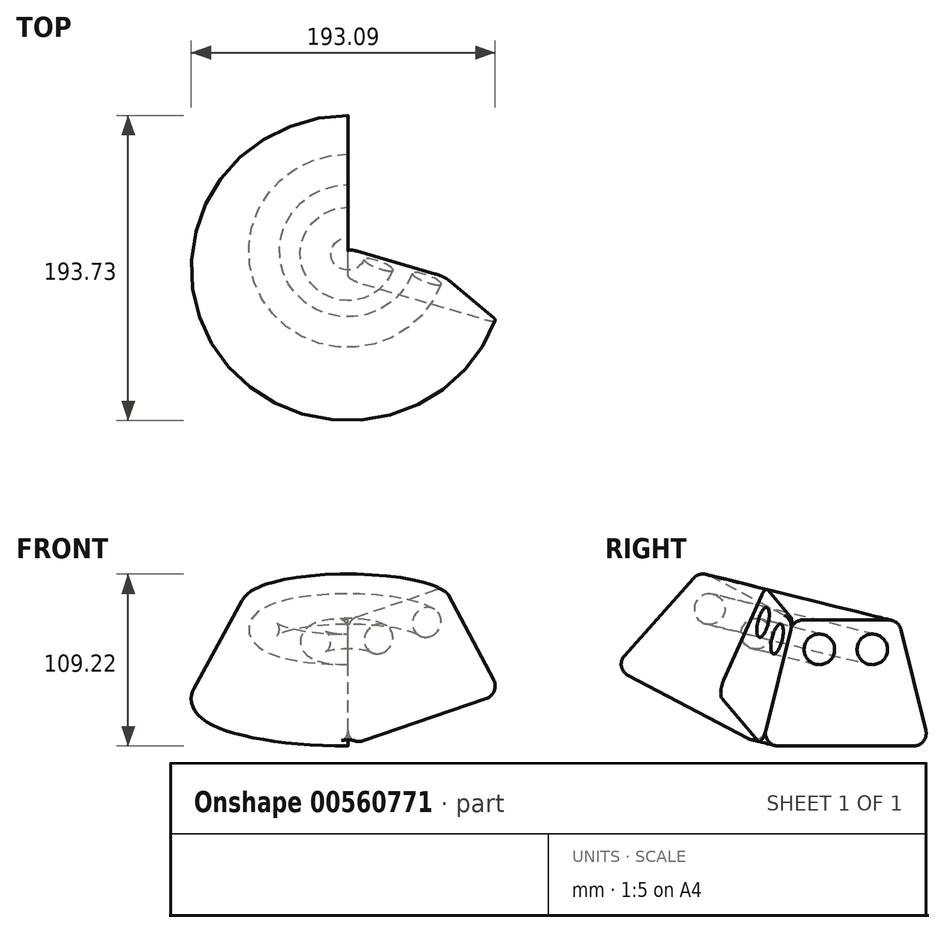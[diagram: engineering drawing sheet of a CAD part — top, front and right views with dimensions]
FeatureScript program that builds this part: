
annotation { "Feature Type Name" : "Feature", "Feature Type Description" : "" }
export const myFeature = defineFeature(function(context is Context, id is Id, definition is map)
    precondition{}
    {
        {
            var Q0;
            Q0=qCreatedBy(makeId("Right.planeOp"),FACE);
            var sketch = newSketch(context, id + "F0", { "sketchPlane" : qUnion([Q0])});
            skLineSegment(sketch, "E0.bottom", {"start": v(10.22, 0) * mm, "end": v(96.29, 0) * mm});
            skLineSegment(sketch, "E0.top", {"start": v(26.06, 80.02) * mm, "end": v(80.44, 80.02) * mm});
            skLineSegment(sketch, "E0.left", {"start": v(2.46, 9.92) * mm, "end": v(18.3, 73.94) * mm});
            skLineSegment(sketch, "E0.right", {"start": v(104.05, 9.92) * mm, "end": v(88.21, 73.94) * mm});
            skLineSegment(sketch, "E1", {"start": v(53.25, 80.02) * mm, "end": v(53.25, 0) * mm, "construction": true});
            skCircle(sketch, "E2", {"center": v(36.46, 61.35) * mm, "radius": 9.7 * mm});
            skCircle(sketch, "E3.MirrorC", {"center": v(70.05, 61.35) * mm, "radius": 9.7 * mm});
            skPoint(sketch, "E4.visualSharp", {"position": v(106.5, 0) * mm});
            skArc(sketch, "E4.filletArc", {"start": v(96.29, 0) * mm, "mid": v(102.59, 3.07) * mm, "end": v(104.05, 9.92) * mm});
            skPoint(sketch, "E5.visualSharp", {"position": v(0, 0) * mm});
            skArc(sketch, "E5.filletArc", {"start": v(2.46, 9.92) * mm, "mid": v(3.92, 3.07) * mm, "end": v(10.22, 0) * mm});
            skPoint(sketch, "E6.visualSharp", {"position": v(19.8, 80.02) * mm});
            skArc(sketch, "E6.filletArc", {"start": v(26.06, 80.02) * mm, "mid": v(21.13, 78.32) * mm, "end": v(18.3, 73.94) * mm});
            skPoint(sketch, "E7.visualSharp", {"position": v(86.7, 80.02) * mm});
            skArc(sketch, "E7.filletArc", {"start": v(88.21, 73.94) * mm, "mid": v(85.38, 78.32) * mm, "end": v(80.44, 80.02) * mm});
            skSolve(sketch);
        }
        {
            var Q0;
            Q0=makeQuery(id+"F0.imprint","IMPRINT",FACE,{"disambiguationData":[TD([[makeQuery(id+"F0.imprint","IMPRINT",EDGE,{"derivedFrom":sQuery(id+"F0.wireOp",EDGE,"E0.bottom")}),1.0]])]});
            var Q1;
            Q1=sQuery(id+"F0.wireOp",EDGE,"E0.left");
            revolve(context, id + "F1", {"entities" : qUnion([Q0]), "axis" : qUnion([Q1]), "revolveType" : RevolveType.ONE_DIRECTION, "angle" : 250 * degree});
        }
    });
